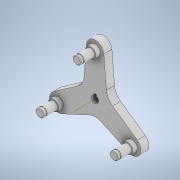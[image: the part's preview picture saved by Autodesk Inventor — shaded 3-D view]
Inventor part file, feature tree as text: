
AUTODESK INVENTOR PART (.ipt)
format: ipt  version: 2020 (Build 240168000, 168)  size: 257,024 bytes
history: native  units: mm
features: extrude x4, sketch x4, revolve x2, projected_geometry x2, other x1, chamfer x1, pattern_circular x1
ambient origin geometry x8: Origin, YZ Plane, XZ Plane, XY Plane, X Axis, Y Axis, Z Axis, Center Point
bodies: Solid1 (feature_tree)
feature tree (15):
  revolve  "Revolution1"  Angle=90.0deg
  extrude  "Extrusion1"  Depth=15.0mm
  sketch  "Sketch4"  dims[d4=45.0mm d6=15.0mm]
  extrude  "Extrusion2"  TaperAngle=120.0deg  [1 undecoded]
  extrude  "Extrusion4"  TaperAngle=60.0deg  [1 undecoded]
  other  "Work Axis2"
  revolve  "Revolution2"  [1 undecoded]
  chamfer  "Chamfer1"  Distance=25.0mm
  pattern_circular  "Circular Pattern1"  [2 undecoded]
  extrude  "Extrusion5"  TaperAngle=0.0deg  [1 undecoded]
  sketch  "Sketch2"  dims[d1=23.0mm d2=90.0deg]
  projected_geometry  "Projected Loop1"
  sketch  "Sketch6"  dims[d7=120.0deg d8=120.0deg]
  projected_geometry  "Projected Loop2"
  sketch  "Sketch7"  dims[d9=60.0deg d10=60.0deg d11=37.075mm d12=25.0mm d13=0.872665mm d14=0.0mm d15=0.0mm d16=30.0mm d17=360.0deg d20=9.0mm d21=16.0mm d22=0.0mm d23=7.0mm d26=12.0mm d27=0.0mm d29=9.0mm d30=90.0deg d31=0.5mm d32=2.0mm d33=45.0deg d34=6.8mm d35=0.9mm d36=3.0mm d37=2.0mm d38=2.2mm d39=2.0mm d40=0.0mm d41=0.0mm]
note: 6 required parameter values undecoded (feature->parameter linkage not recoverable at this tier; creation-order binding heuristic only, values carry confidence <= 0.55)